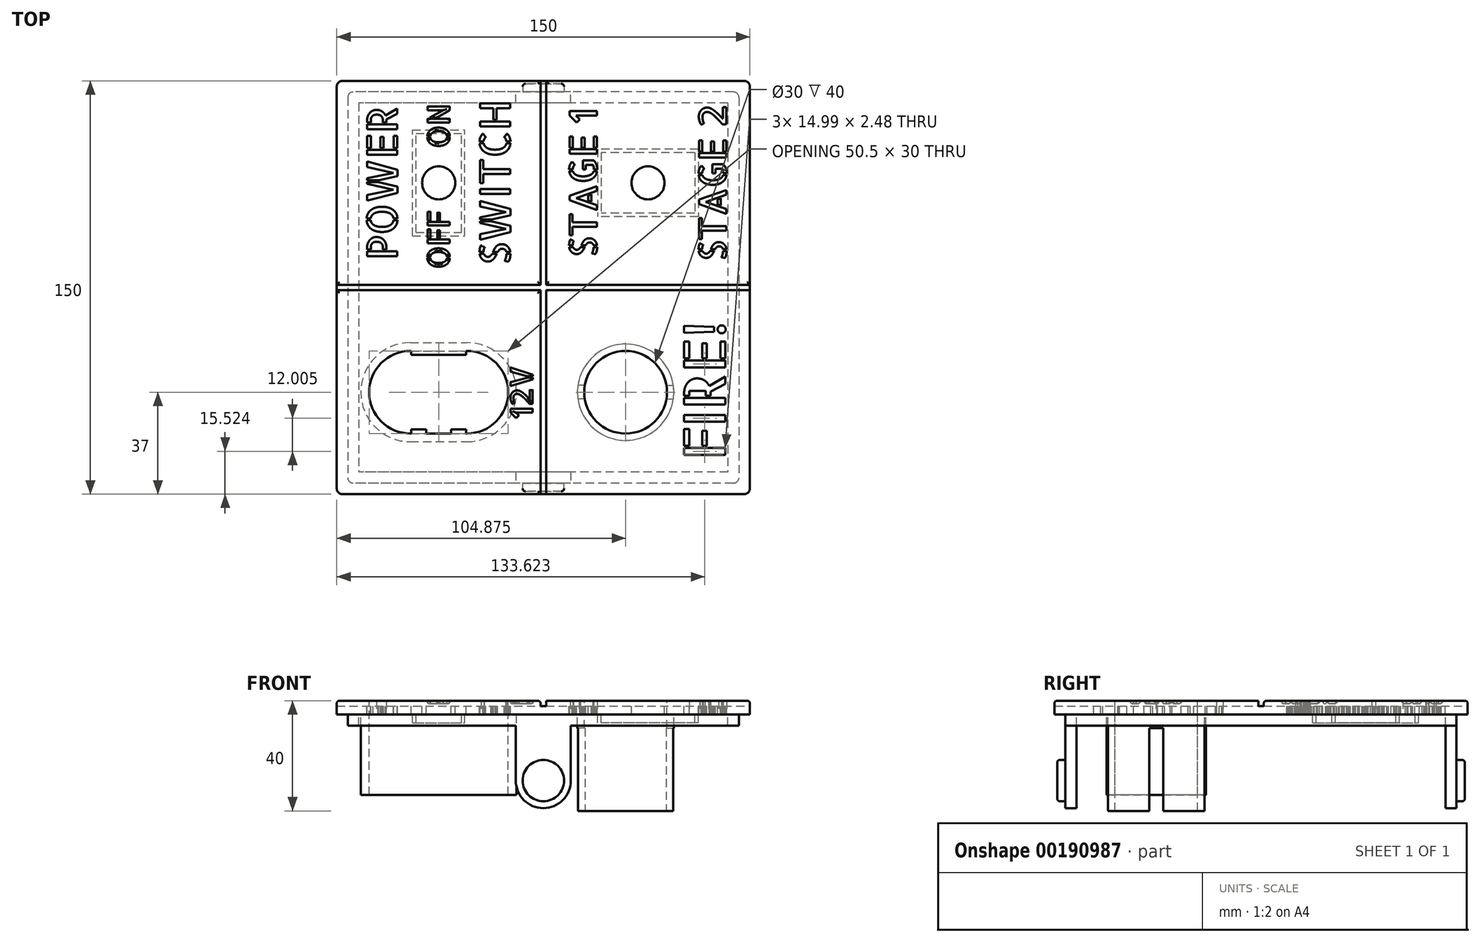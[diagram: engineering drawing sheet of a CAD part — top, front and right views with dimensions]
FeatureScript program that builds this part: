
annotation { "Feature Type Name" : "Feature", "Feature Type Description" : "" }
export const myFeature = defineFeature(function(context is Context, id is Id, definition is map)
    precondition{}
    {
        {
            var Q0;
            Q0=qCreatedBy(makeId("Top.planeOp"),FACE);
            var sketch = newSketch(context, id + "F0", { "sketchPlane" : qUnion([Q0])});
            skLineSegment(sketch, "E0.bottom", {"start": v(75, 75) * mm, "end": v(-75, 75) * mm});
            skLineSegment(sketch, "E0.top", {"start": v(75, -75) * mm, "end": v(-75, -75) * mm});
            skLineSegment(sketch, "E0.left", {"start": v(75, 75) * mm, "end": v(75, -75) * mm});
            skLineSegment(sketch, "E0.right", {"start": v(-75, 75) * mm, "end": v(-75, -75) * mm});
            skPoint(sketch, "E0.middle", {"position": v(0, 0) * mm});
            skSolve(sketch);
        }
        {
            var Q0;
            Q0=makeQuery(id+"F0.imprint","IMPRINT",FACE,{"disambiguationData":[TD([[makeQuery(id+"F0.imprint","IMPRINT",EDGE,{"derivedFrom":sQuery(id+"F0.wireOp",EDGE,"E0.bottom")}),1.0]])]});
            extrude(context, id + "F1", {"entities" : qUnion([Q0]), "depth" : 5 * mm});
        }
        {
            var Q0;
            Q0=makeQuery(id+"F1.opExtrude","CAP_FACE",FACE,{"disambiguationData":[OSD([sQuery(id+"F0.wireOp",EDGE,"E0.bottom"),sQuery(id+"F0.wireOp",EDGE,"E0.top"),sQuery(id+"F0.wireOp",EDGE,"E0.left"),sQuery(id+"F0.wireOp",EDGE,"E0.right")])],"isStart":true});
            var sketch = newSketch(context, id + "F2", { "sketchPlane" : qUnion([Q0])});
            skLineSegment(sketch, "E1.0", {"start": v(-71, -71) * mm, "end": v(-71, 71) * mm});
            skLineSegment(sketch, "E1.1", {"start": v(71, -71) * mm, "end": v(-71, -71) * mm});
            skLineSegment(sketch, "E1.2", {"start": v(71, -71) * mm, "end": v(71, 71) * mm});
            skLineSegment(sketch, "E1.3", {"start": v(71, 71) * mm, "end": v(-71, 71) * mm});
            skLineSegment(sketch, "E2.0", {"start": v(-67, -67) * mm, "end": v(-67, 67) * mm});
            skLineSegment(sketch, "E2.1", {"start": v(67, -67) * mm, "end": v(-67, -67) * mm});
            skLineSegment(sketch, "E2.2", {"start": v(67, -67) * mm, "end": v(67, 67) * mm});
            skLineSegment(sketch, "E2.3", {"start": v(67, 67) * mm, "end": v(-67, 67) * mm});
            skSolve(sketch);
        }
        {
            var Q0;
            Q0=makeQuery(id+"F2.imprint","IMPRINT",FACE,{"disambiguationData":[TD([[makeQuery(id+"F2.imprint","IMPRINT",EDGE,{"derivedFrom":sQuery(id+"F2.wireOp",EDGE,"E1.0")}),-1.0]])]});
            extrude(context, id + "F3", {"entities" : qUnion([Q0]), "operationType" : NewBodyOperationType.ADD, "depth" : 4 * mm});
        }
        {
            var Q0;
            Q0=makeQuery(id+"F3.opExtrude","CAP_FACE",FACE,{"disambiguationData":[OSD([sQuery(id+"F2.wireOp",EDGE,"E1.0"),sQuery(id+"F2.wireOp",EDGE,"E1.1"),sQuery(id+"F2.wireOp",EDGE,"E1.2"),sQuery(id+"F2.wireOp",EDGE,"E1.3"),sQuery(id+"F2.wireOp",EDGE,"E2.0"),sQuery(id+"F2.wireOp",EDGE,"E2.1"),sQuery(id+"F2.wireOp",EDGE,"E2.2"),sQuery(id+"F2.wireOp",EDGE,"E2.3")])],"isStart":false});
            var sketch = newSketch(context, id + "F4", { "sketchPlane" : qUnion([Q0])});
            skLineSegment(sketch, "E3.bottom", {"start": v(-10, -67) * mm, "end": v(10, -67) * mm});
            skLineSegment(sketch, "E3.top", {"start": v(-10, -71) * mm, "end": v(10, -71) * mm});
            skLineSegment(sketch, "E3.left", {"start": v(-10, -67) * mm, "end": v(-10, -71) * mm});
            skLineSegment(sketch, "E3.right", {"start": v(10, -67) * mm, "end": v(10, -71) * mm});
            skLineSegment(sketch, "E4.bottom", {"start": v(-67, 10) * mm, "end": v(-71, 10) * mm});
            skLineSegment(sketch, "E4.top", {"start": v(-67, -10) * mm, "end": v(-71, -10) * mm});
            skLineSegment(sketch, "E4.left", {"start": v(-67, 10) * mm, "end": v(-67, -10) * mm});
            skLineSegment(sketch, "E4.right", {"start": v(-71, 10) * mm, "end": v(-71, -10) * mm});
            skLineSegment(sketch, "E5.bottom", {"start": v(10, 67) * mm, "end": v(-10, 67) * mm});
            skLineSegment(sketch, "E5.top", {"start": v(10, 71) * mm, "end": v(-10, 71) * mm});
            skLineSegment(sketch, "E5.left", {"start": v(10, 67) * mm, "end": v(10, 71) * mm});
            skLineSegment(sketch, "E5.right", {"start": v(-10, 67) * mm, "end": v(-10, 71) * mm});
            skLineSegment(sketch, "E6.bottom", {"start": v(67, 10) * mm, "end": v(71, 10) * mm});
            skLineSegment(sketch, "E6.top", {"start": v(67, -10) * mm, "end": v(71, -10) * mm});
            skLineSegment(sketch, "E6.left", {"start": v(67, 10) * mm, "end": v(67, -10) * mm});
            skLineSegment(sketch, "E6.right", {"start": v(71, 10) * mm, "end": v(71, -10) * mm});
            skSolve(sketch);
        }
        {
            var Q0;
            Q0=makeQuery(id+"F4.imprint","IMPRINT",FACE,{"disambiguationData":[TD([[makeQuery(id+"F4.imprint","IMPRINT",EDGE,{"derivedFrom":sQuery(id+"F4.wireOp",EDGE,"E5.bottom")}),-1.0]])]});
            var Q1;
            Q1=makeQuery(id+"F4.imprint","IMPRINT",FACE,{"disambiguationData":[TD([[makeQuery(id+"F4.imprint","IMPRINT",EDGE,{"derivedFrom":sQuery(id+"F4.wireOp",EDGE,"E3.bottom")}),1.0]])]});
            extrude(context, id + "F5", {"entities" : qUnion([Q0, Q1]), "operationType" : NewBodyOperationType.ADD, "depth" : 30 * mm});
        }
        {
            var Q0;
            Q0=makeQuery(id+"F5.opExtrude","CAP_EDGE",EDGE,{"disambiguationData":[OSD([sQuery(id+"F4.wireOp",EDGE,"E3.left")])],"isStart":false});
            var Q1;
            Q1=makeQuery(id+"F5.opExtrude","CAP_EDGE",EDGE,{"disambiguationData":[OSD([sQuery(id+"F4.wireOp",EDGE,"E3.right")])],"isStart":false});
            var Q2;
            Q2=makeQuery(id+"F5.opExtrude","CAP_EDGE",EDGE,{"disambiguationData":[OSD([sQuery(id+"F4.wireOp",EDGE,"E5.left")])],"isStart":false});
            var Q3;
            Q3=makeQuery(id+"F5.opExtrude","CAP_EDGE",EDGE,{"disambiguationData":[OSD([sQuery(id+"F4.wireOp",EDGE,"E5.right")])],"isStart":false});
            fillet(context, id + "F6", {"entities" : qUnion([Q0, Q1, Q2, Q3]), "radius" : 10 * mm, "tangentPropagation" : true, "allowEdgeOverflow" : false});
        }
        {
            var Q0;
            Q0=makeQuery(id+"F5.boolean.opBoolean","MERGE",FACE,{"derivedFrom":[makeQuery(id+"F3.opExtrude","SWEPT_FACE",FACE,{"disambiguationData":[OSD([sQuery(id+"F2.wireOp",EDGE,"E1.1")])]}),makeQuery(id+"F5.opExtrude","SWEPT_FACE",FACE,{"disambiguationData":[OSD([sQuery(id+"F4.wireOp",EDGE,"E3.top")])]})]});
            var sketch = newSketch(context, id + "F7", { "sketchPlane" : qUnion([Q0])});
            skCircle(sketch, "E7", {"center": v(0, -24) * mm, "radius": 7.5 * mm});
            skSolve(sketch);
        }
        {
            var Q0;
            Q0=makeQuery(id+"F7.imprint","IMPRINT",FACE,{"disambiguationData":[TD([[makeQuery(id+"F7.imprint","IMPRINT",EDGE,{"derivedFrom":sQuery(id+"F7.wireOp",EDGE,"E7")}),1.0]])]});
            extrude(context, id + "F8", {"entities" : qUnion([Q0]), "operationType" : NewBodyOperationType.ADD, "depth" : 3 * mm});
        }
        {
            var Q0;
            Q0=makeQuery(id+"F5.boolean.opBoolean","MERGE",FACE,{"derivedFrom":[makeQuery(id+"F3.opExtrude","SWEPT_FACE",FACE,{"disambiguationData":[OSD([sQuery(id+"F2.wireOp",EDGE,"E1.3")])]}),makeQuery(id+"F5.opExtrude","SWEPT_FACE",FACE,{"disambiguationData":[OSD([sQuery(id+"F4.wireOp",EDGE,"E5.top")])]})]});
            var sketch = newSketch(context, id + "F9", { "sketchPlane" : qUnion([Q0])});
            skCircle(sketch, "E8", {"center": v(0, -24) * mm, "radius": 7.5 * mm});
            skSolve(sketch);
        }
        {
            var Q0;
            Q0=makeQuery(id+"F9.imprint","IMPRINT",FACE,{"disambiguationData":[TD([[makeQuery(id+"F9.imprint","IMPRINT",EDGE,{"derivedFrom":sQuery(id+"F9.wireOp",EDGE,"E8")}),1.0]])]});
            extrude(context, id + "F10", {"entities" : qUnion([Q0]), "operationType" : NewBodyOperationType.ADD, "depth" : 3 * mm});
        }
        {
            var Q0;
            Q0=makeQuery(id+"F10.opExtrude","CAP_EDGE",EDGE,{"disambiguationData":[OSD([sQuery(id+"F9.wireOp",EDGE,"E8")])],"isStart":false});
            var Q1;
            Q1=makeQuery(id+"F8.opExtrude","CAP_EDGE",EDGE,{"disambiguationData":[OSD([sQuery(id+"F7.wireOp",EDGE,"E7")])],"isStart":false});
            fillet(context, id + "F11", {"entities" : qUnion([Q0, Q1]), "radius" : 1 * mm, "tangentPropagation" : true, "allowEdgeOverflow" : false});
        }
        {
            var Q0;
            Q0=makeQuery(id+"F1.opExtrude","CAP_FACE",FACE,{"disambiguationData":[OSD([sQuery(id+"F0.wireOp",EDGE,"E0.bottom"),sQuery(id+"F0.wireOp",EDGE,"E0.top"),sQuery(id+"F0.wireOp",EDGE,"E0.left"),sQuery(id+"F0.wireOp",EDGE,"E0.right")])],"isStart":false});
            var sketch = newSketch(context, id + "F12", { "sketchPlane" : qUnion([Q0])});
            skLineSegment(sketch, "E9", {"start": v(75, 75) * mm, "end": v(0, 75) * mm});
            skCircle(sketch, "E10", {"center": v(38, 38) * mm, "radius": 6 * mm});
            skCircle(sketch, "E11", {"center": v(29.87, -38) * mm, "radius": 15 * mm});
            skLineSegment(sketch, "E12", {"start": v(38, -38) * mm, "end": v(29.87, -38) * mm});
            skCircle(sketch, "E13", {"center": v(-38, 38) * mm, "radius": 6 * mm});
            skLineSegment(sketch, "E14.0", {"start": v(1, -75) * mm, "end": v(1, -1) * mm});
            skLineSegment(sketch, "E15.0", {"start": v(-1, -75) * mm, "end": v(-1, -1) * mm});
            skLineSegment(sketch, "E16.0", {"start": v(-75, -1) * mm, "end": v(-1, -1) * mm});
            skLineSegment(sketch, "E17.0", {"start": v(-75, 1) * mm, "end": v(-1, 1) * mm});
            skLineSegment(sketch, "E18.trimOffspring", {"start": v(-1, 1) * mm, "end": v(-1, 75) * mm});
            skLineSegment(sketch, "E19.trimOffspring", {"start": v(1, 1) * mm, "end": v(75, 1) * mm});
            skLineSegment(sketch, "E20.trimOffspring", {"start": v(1, -1) * mm, "end": v(75, -1) * mm});
            skLineSegment(sketch, "E21.trimOffspring", {"start": v(1, 1) * mm, "end": v(1, 75) * mm});
            skLineSegment(sketch, "E22.bottom", {"start": v(-48.25, -53) * mm, "end": v(-27.75, -53) * mm});
            skLineSegment(sketch, "E22.top", {"start": v(-48.25, -23) * mm, "end": v(-27.75, -23) * mm});
            skArc(sketch, "E23", {"start": v(-48.25, -23) * mm, "mid": v(-63.25, -38) * mm, "end": v(-48.25, -53) * mm});
            skArc(sketch, "E24", {"start": v(-27.75, -53) * mm, "mid": v(-12.75, -38) * mm, "end": v(-27.75, -23) * mm});
            skPoint(sketch, "E25", {"position": v(-63.25, -38) * mm});
            skPoint(sketch, "E26", {"position": v(-12.75, -38) * mm});
            skArc(sketch, "E27.0", {"start": v(-48.25, -20) * mm, "mid": v(-66.25, -38) * mm, "end": v(-48.25, -56) * mm});
            skLineSegment(sketch, "E27.1", {"start": v(-48.25, -20) * mm, "end": v(-27.75, -20) * mm});
            skArc(sketch, "E27.2", {"start": v(-27.75, -56) * mm, "mid": v(-9.75, -38) * mm, "end": v(-27.75, -20) * mm});
            skLineSegment(sketch, "E27.3", {"start": v(-48.25, -56) * mm, "end": v(-27.75, -56) * mm});
            skPoint(sketch, "E28", {"position": v(-38, -38) * mm});
            skPoint(sketch, "E29", {"position": v(-38, -23) * mm});
            skPoint(sketch, "E30", {"position": v(-38, -53) * mm});
            skLineSegment(sketch, "E31.bottom", {"start": v(-48, -24.5) * mm, "end": v(-28, -24.5) * mm});
            skLineSegment(sketch, "E31.left", {"start": v(-48, -24.5) * mm, "end": v(-48, -23) * mm});
            skLineSegment(sketch, "E31.right", {"start": v(-28, -24.5) * mm, "end": v(-28, -23) * mm});
            skLineSegment(sketch, "E32.bottom", {"start": v(-48, -51.5) * mm, "end": v(-42.5, -51.5) * mm});
            skLineSegment(sketch, "E32.left", {"start": v(-48, -51.5) * mm, "end": v(-48, -53) * mm});
            skLineSegment(sketch, "E32.right", {"start": v(-28, -51.5) * mm, "end": v(-28, -53) * mm});
            skLineSegment(sketch, "E33.left", {"start": v(-42.5, -51.5) * mm, "end": v(-42.5, -53) * mm});
            skLineSegment(sketch, "E33.right", {"start": v(-33.5, -51.5) * mm, "end": v(-33.5, -53) * mm});
            skLineSegment(sketch, "E34.trimOffspring", {"start": v(-33.5, -51.5) * mm, "end": v(-28, -51.5) * mm});
            skSolve(sketch);
        }
        {
            var Q0;
            Q0=makeQuery(id+"F12.imprint","IMPRINT",FACE,{"disambiguationData":[TD([[makeQuery(id+"F12.imprint","IMPRINT",EDGE,{"derivedFrom":sQuery(id+"F12.wireOp",EDGE,"E10")}),1.0]])]});
            var Q1;
            Q1=makeQuery(id+"F12.imprint","IMPRINT",FACE,{"disambiguationData":[TD([[makeQuery(id+"F12.imprint","IMPRINT",EDGE,{"derivedFrom":sQuery(id+"F12.wireOp",EDGE,"E11")}),1.0]])]});
            var Q2;
            Q2=makeQuery(id+"F12.imprint","IMPRINT",FACE,{"disambiguationData":[TD([[makeQuery(id+"F12.imprint","IMPRINT",EDGE,{"derivedFrom":sQuery(id+"F12.wireOp",EDGE,"E13")}),1.0]])]});
            var Q3;
            Q3=makeQuery(id+"F12.imprint","IMPRINT",FACE,{"disambiguationData":[TD([[makeQuery(id+"F12.imprint","IMPRINT",EDGE,{"derivedFrom":sQuery(id+"F12.wireOp",EDGE,"E22.bottom")}),1.0]])]});
            extrude(context, id + "F13", {"entities" : qUnion([Q0, Q1, Q2, Q3]), "operationType" : NewBodyOperationType.REMOVE, "oppositeDirection" : true, "depth" : 25 * mm});
        }
        {
            var Q0;
            Q0=makeQuery(id+"F3.boolean.opBoolean","SPLIT",FACE,{"disambiguationData":[TD([makeQuery(id+"F3.opExtrude","SWEPT_FACE",FACE,{"disambiguationData":[OSD([sQuery(id+"F2.wireOp",EDGE,"E2.0")])]})])],"derivedFrom":makeQuery(id+"F1.opExtrude","CAP_FACE",FACE,{"disambiguationData":[OSD([sQuery(id+"F0.wireOp",EDGE,"E0.bottom"),sQuery(id+"F0.wireOp",EDGE,"E0.top"),sQuery(id+"F0.wireOp",EDGE,"E0.left"),sQuery(id+"F0.wireOp",EDGE,"E0.right")])],"isStart":true})});
            var sketch = newSketch(context, id + "F14", { "sketchPlane" : qUnion([Q0])});
            skLineSegment(sketch, "E35.bottom", {"start": v(55, -49) * mm, "end": v(21, -49) * mm});
            skLineSegment(sketch, "E35.top", {"start": v(55, -27) * mm, "end": v(21, -27) * mm});
            skLineSegment(sketch, "E35.left", {"start": v(55, -49) * mm, "end": v(55, -27) * mm});
            skLineSegment(sketch, "E35.right", {"start": v(21, -49) * mm, "end": v(21, -27) * mm});
            skPoint(sketch, "E35.middle", {"position": v(38, -38) * mm});
            skLineSegment(sketch, "E36.0", {"start": v(19.75, -50.25) * mm, "end": v(19.75, -25.75) * mm});
            skLineSegment(sketch, "E36.1", {"start": v(56.25, -50.25) * mm, "end": v(19.75, -50.25) * mm});
            skLineSegment(sketch, "E36.2", {"start": v(56.25, -50.25) * mm, "end": v(56.25, -25.75) * mm});
            skLineSegment(sketch, "E36.3", {"start": v(56.25, -25.75) * mm, "end": v(19.75, -25.75) * mm});
            skCircle(sketch, "E37", {"center": v(29.87, 38) * mm, "radius": 15 * mm});
            skCircle(sketch, "E38", {"center": v(29.87, 38) * mm, "radius": 17.5 * mm});
            skPoint(sketch, "E39.middle", {"position": v(-38, -38) * mm});
            skLineSegment(sketch, "E40.bottom", {"start": v(-46.25, -20) * mm, "end": v(-29.75, -20) * mm});
            skLineSegment(sketch, "E40.top", {"start": v(-46.25, -56) * mm, "end": v(-29.75, -56) * mm});
            skLineSegment(sketch, "E40.left", {"start": v(-46.25, -20) * mm, "end": v(-46.25, -56) * mm});
            skLineSegment(sketch, "E40.right", {"start": v(-29.75, -20) * mm, "end": v(-29.75, -56) * mm});
            skLineSegment(sketch, "E41.0", {"start": v(-47.5, -18.75) * mm, "end": v(-47.5, -57.25) * mm});
            skLineSegment(sketch, "E41.1", {"start": v(-47.5, -18.75) * mm, "end": v(-28.5, -18.75) * mm});
            skLineSegment(sketch, "E41.2", {"start": v(-28.5, -18.75) * mm, "end": v(-28.5, -57.25) * mm});
            skLineSegment(sketch, "E41.3", {"start": v(-47.5, -57.25) * mm, "end": v(-28.5, -57.25) * mm});
            skSolve(sketch);
        }
        {
            var Q0;
            Q0=makeQuery(id+"F14.imprint","IMPRINT",FACE,{"disambiguationData":[TD([[makeQuery(id+"F14.imprint","IMPRINT",EDGE,{"derivedFrom":sQuery(id+"F14.wireOp",EDGE,"E35.bottom")}),1.0]])]});
            var Q1;
            Q1=makeQuery(id+"F14.imprint","IMPRINT",FACE,{"disambiguationData":[TD([[makeQuery(id+"F14.imprint","IMPRINT",EDGE,{"derivedFrom":sQuery(id+"F14.wireOp",EDGE,"E39.bottom")}),1.0]])]});
            var Q2;
            Q2=makeQuery(id+"F14.imprint","IMPRINT",FACE,{"disambiguationData":[TD([[makeQuery(id+"F14.imprint","IMPRINT",EDGE,{"derivedFrom":sQuery(id+"F14.wireOp",EDGE,"E39.top")}),-1.0]])]});
            var Q3;
            Q3=makeQuery(id+"F14.imprint","IMPRINT",FACE,{"disambiguationData":[TD([[makeQuery(id+"F14.imprint","IMPRINT",EDGE,{"derivedFrom":sQuery(id+"F14.wireOp",EDGE,"E40.bottom")}),1.0]])]});
            extrude(context, id + "F15", {"entities" : qUnion([Q0, Q1, Q2, Q3]), "operationType" : NewBodyOperationType.ADD, "depth" : 3 * mm});
        }
        {
            var Q0;
            Q0=makeQuery(id+"F1.opExtrude","CAP_FACE",FACE,{"disambiguationData":[OSD([sQuery(id+"F0.wireOp",EDGE,"E0.bottom"),sQuery(id+"F0.wireOp",EDGE,"E0.top"),sQuery(id+"F0.wireOp",EDGE,"E0.left"),sQuery(id+"F0.wireOp",EDGE,"E0.right")])],"isStart":false});
            var sketch = newSketch(context, id + "F16", { "sketchPlane" : qUnion([Q0])});
            skCircle(sketch, "E42", {"center": v(38, 38) * mm, "radius": 6 * mm});
            skLineSegment(sketch, "E43", {"start": v(38, 38) * mm, "end": v(32, 38) * mm});
            skLineSegment(sketch, "E44", {"start": v(38, 38) * mm, "end": v(44, 38) * mm});
            skLineSegment(sketch, "E45", {"start": v(44, 38) * mm, "end": v(56.5, 38) * mm});
            skLineSegment(sketch, "E46", {"start": v(32, 38) * mm, "end": v(19.5, 38) * mm});
            skText(sketch, "E47", { "text": "STAGE 2", "fontName": "AllertaStencil-Regular.ttf"});
            skText(sketch, "E48", { "text": "STAGE 1", "fontName": "AllertaStencil-Regular.ttf"});
            skText(sketch, "E49", { "text": "FIRE!", "fontName": "AllertaStencil-Regular.ttf"});
            skLineSegment(sketch, "E50", {"start": v(44.87, -37.48) * mm, "end": v(51.12, -37.48) * mm});
            skPoint(sketch, "E51", {"position": v(58.62, -37.48) * mm});
            skLineSegment(sketch, "E52", {"start": v(66.12, -37.48) * mm, "end": v(44.87, -37.48) * mm});
            skPoint(sketch, "E53", {"position": v(40.5, -37.48) * mm});
            skLineSegment(sketch, "E54", {"start": v(0, -75) * mm, "end": v(75, 0) * mm});
            skLineSegment(sketch, "E55", {"start": v(75, -75) * mm, "end": v(0, 0) * mm});
            skPoint(sketch, "E56.orphan", {"position": v(14.88, -37.48) * mm});
            skLineSegment(sketch, "E57.trimOffspring", {"start": v(40.5, -37.48) * mm, "end": v(37.52, -37.48) * mm});
            skText(sketch, "E58", { "text": "POWER", "fontName": "AllertaStencil-Regular.ttf"});
            skLineSegment(sketch, "E59", {"start": v(-38, 38) * mm, "end": v(-53, 38) * mm});
            skLineSegment(sketch, "E60", {"start": v(-38, 38) * mm, "end": v(-23, 38) * mm});
            skText(sketch, "E61", { "text": "SWITCH", "fontName": "AllertaStencil-Regular.ttf"});
            const initialGuessF16  = {"E47": [0.0665, 0.00959, 0, 1, 0.01], "E48": [0.0195, 0.01099, 0, 1, 0.01], "E49": [0.06612, -0.06265, 0, 1, 0.015], "E58": [-0.053, 0.01, 0, 1, 0.011], "E61": [-0.012, 0.00816, 0, 1, 0.011]};
            skSetInitialGuess(sketch, initialGuessF16);
            skSolve(sketch);
        }
        {
            var Q0;
            Q0 = qSketchRegion(id + "F16", true);
            extrude(context, id + "F17", {"entities" : qUnion([Q0]), "operationType" : NewBodyOperationType.REMOVE, "oppositeDirection" : true, "depth" : 25 * mm});
        }
        {
            var Q0;
            Q0=makeQuery(id+"F14.imprint","IMPRINT",FACE,{"disambiguationData":[TD([[makeQuery(id+"F14.imprint","IMPRINT",EDGE,{"derivedFrom":sQuery(id+"F14.wireOp",EDGE,"E37")}),1.0]])]});
            extrude(context, id + "F18", {"entities" : qUnion([Q0]), "operationType" : NewBodyOperationType.ADD, "depth" : 35 * mm});
        }
        {
            var Q0;
            Q0=makeQuery(id+"F18.opExtrude","CAP_FACE",FACE,{"disambiguationData":[OSD([sQuery(id+"F14.wireOp",EDGE,"E37"),sQuery(id+"F14.wireOp",EDGE,"E38")])],"isStart":false});
            var sketch = newSketch(context, id + "F19", { "sketchPlane" : qUnion([Q0])});
            skCircle(sketch, "E62", {"center": v(29.87, 38) * mm, "radius": 16.25 * mm});
            skPoint(sketch, "E63", {"position": v(46.12, 38) * mm});
            skPoint(sketch, "E64", {"position": v(13.62, 38) * mm});
            skLineSegment(sketch, "E65.bottom", {"start": v(15.62, 35.5) * mm, "end": v(11.62, 35.5) * mm});
            skLineSegment(sketch, "E65.top", {"start": v(15.62, 40.5) * mm, "end": v(11.62, 40.5) * mm});
            skLineSegment(sketch, "E65.left", {"start": v(15.62, 35.5) * mm, "end": v(15.62, 40.5) * mm});
            skLineSegment(sketch, "E65.right", {"start": v(11.62, 35.5) * mm, "end": v(11.62, 40.5) * mm});
            skLineSegment(sketch, "E66.bottom", {"start": v(44.12, 35.5) * mm, "end": v(48.12, 35.5) * mm});
            skLineSegment(sketch, "E66.top", {"start": v(44.12, 40.5) * mm, "end": v(48.12, 40.5) * mm});
            skLineSegment(sketch, "E66.left", {"start": v(44.12, 35.5) * mm, "end": v(44.12, 40.5) * mm});
            skLineSegment(sketch, "E66.right", {"start": v(48.12, 35.5) * mm, "end": v(48.12, 40.5) * mm});
            skSolve(sketch);
        }
        {
            var Q0;
            {var subQ0=sQuery(id+"F19.wireOp",EDGE,"E65.top");var subQ1=sQuery(id+"F19.wireOp",EDGE,"E62");var subQ2=makeQuery(id+"F19.imprint","INTERSECT",VERTEX,{"derivedFrom":[subQ1,subQ0]});Q0=makeQuery(id+"F19.imprint","IMPRINT",FACE,{"disambiguationData":[TD([[makeQuery(id+"F19.imprint","IMPRINT",EDGE,{"disambiguationData":[TD([[subQ2,-1.0]])],"derivedFrom":subQ1}),1.0]])]});}
            var Q1;
            {var subQ0=sQuery(id+"F19.wireOp",EDGE,"E65.top");var subQ1=sQuery(id+"F19.wireOp",EDGE,"E62");var subQ2=makeQuery(id+"F19.imprint","INTERSECT",VERTEX,{"derivedFrom":[subQ1,subQ0]});Q1=makeQuery(id+"F19.imprint","IMPRINT",FACE,{"disambiguationData":[TD([[makeQuery(id+"F19.imprint","IMPRINT",EDGE,{"disambiguationData":[TD([[subQ2,-1.0]])],"derivedFrom":subQ1}),-1.0]])]});}
            var Q2;
            {var subQ0=sQuery(id+"F19.wireOp",EDGE,"E66.top");var subQ1=sQuery(id+"F19.wireOp",EDGE,"E62");var subQ2=makeQuery(id+"F19.imprint","INTERSECT",VERTEX,{"derivedFrom":[subQ1,subQ0]});Q2=makeQuery(id+"F19.imprint","IMPRINT",FACE,{"disambiguationData":[TD([[makeQuery(id+"F19.imprint","IMPRINT",EDGE,{"disambiguationData":[TD([[subQ2,1.0]])],"derivedFrom":subQ1}),1.0]])]});}
            var Q3;
            {var subQ0=sQuery(id+"F19.wireOp",EDGE,"E66.top");var subQ1=sQuery(id+"F19.wireOp",EDGE,"E62");var subQ2=makeQuery(id+"F19.imprint","INTERSECT",VERTEX,{"derivedFrom":[subQ1,subQ0]});Q3=makeQuery(id+"F19.imprint","IMPRINT",FACE,{"disambiguationData":[TD([[makeQuery(id+"F19.imprint","IMPRINT",EDGE,{"disambiguationData":[TD([[subQ2,1.0]])],"derivedFrom":subQ1}),-1.0]])]});}
            extrude(context, id + "F20", {"entities" : qUnion([Q0, Q1, Q2, Q3]), "operationType" : NewBodyOperationType.REMOVE, "oppositeDirection" : true, "depth" : 30 * mm});
        }
        {
            var Q0;
            {var subQ8=sQuery(id+"F12.wireOp",EDGE,"E14.0");Q0=makeQuery(id+"F12.imprint","IMPRINT",FACE,{"disambiguationData":[TD([[makeQuery(id+"F12.imprint","IMPRINT",EDGE,{"derivedFrom":subQ8}),1.0]])]});}
            extrude(context, id + "F21", {"entities" : qUnion([Q0]), "operationType" : NewBodyOperationType.REMOVE, "oppositeDirection" : true, "depth" : 2 * mm});
        }
        {
            var Q0;
            Q0=makeQuery(id+"F21.boolean.opBoolean","COPY",EDGE,{"derivedFrom":makeQuery(id+"F21.opExtrude","CAP_EDGE",EDGE,{"disambiguationData":[OSD([sQuery(id+"F12.wireOp",EDGE,"E20.trimOffspring")])],"isStart":true})});
            var Q1;
            Q1=makeQuery(id+"F21.boolean.opBoolean","COPY",EDGE,{"derivedFrom":makeQuery(id+"F21.opExtrude","CAP_EDGE",EDGE,{"disambiguationData":[OSD([sQuery(id+"F12.wireOp",EDGE,"E16.0")])],"isStart":true})});
            var Q2;
            Q2=makeQuery(id+"F21.boolean.opBoolean","COPY",EDGE,{"derivedFrom":makeQuery(id+"F21.opExtrude","CAP_EDGE",EDGE,{"disambiguationData":[OSD([sQuery(id+"F12.wireOp",EDGE,"E15.0")])],"isStart":true})});
            var Q3;
            Q3=makeQuery(id+"F21.boolean.opBoolean","COPY",EDGE,{"derivedFrom":makeQuery(id+"F21.opExtrude","CAP_EDGE",EDGE,{"disambiguationData":[OSD([sQuery(id+"F12.wireOp",EDGE,"E17.0")])],"isStart":true})});
            var Q4;
            Q4=makeQuery(id+"F21.boolean.opBoolean","COPY",EDGE,{"derivedFrom":makeQuery(id+"F21.opExtrude","CAP_EDGE",EDGE,{"disambiguationData":[OSD([sQuery(id+"F12.wireOp",EDGE,"E18.trimOffspring")])],"isStart":true})});
            var Q5;
            Q5=makeQuery(id+"F21.boolean.opBoolean","COPY",EDGE,{"derivedFrom":makeQuery(id+"F21.opExtrude","CAP_EDGE",EDGE,{"disambiguationData":[OSD([sQuery(id+"F12.wireOp",EDGE,"E21.trimOffspring")])],"isStart":true})});
            var Q6;
            Q6=makeQuery(id+"F21.boolean.opBoolean","COPY",EDGE,{"derivedFrom":makeQuery(id+"F21.opExtrude","CAP_EDGE",EDGE,{"disambiguationData":[OSD([sQuery(id+"F12.wireOp",EDGE,"E19.trimOffspring")])],"isStart":true})});
            var Q7;
            Q7=makeQuery(id+"F21.boolean.opBoolean","COPY",EDGE,{"derivedFrom":makeQuery(id+"F21.opExtrude","CAP_EDGE",EDGE,{"disambiguationData":[OSD([sQuery(id+"F12.wireOp",EDGE,"E14.0")])],"isStart":true})});
            var Q8;
            {var subQ0=sQuery(id+"F0.wireOp",EDGE,"E0.bottom");var subQ1=sQuery(id+"F0.wireOp",EDGE,"E0.right");Q8=makeQuery(id+"F21.boolean.opBoolean","SPLIT",EDGE,{"disambiguationData":[TD([makeQuery(id+"F1.opExtrude","SWEPT_FACE",FACE,{"disambiguationData":[OSD([subQ1])]})])],"derivedFrom":makeQuery(id+"F1.opExtrude","CAP_EDGE",EDGE,{"disambiguationData":[OSD([subQ0])],"isStart":false})});}
            var Q9;
            {var subQ0=sQuery(id+"F0.wireOp",EDGE,"E0.bottom");var subQ1=sQuery(id+"F0.wireOp",EDGE,"E0.left");Q9=makeQuery(id+"F21.boolean.opBoolean","SPLIT",EDGE,{"disambiguationData":[TD([makeQuery(id+"F1.opExtrude","SWEPT_FACE",FACE,{"disambiguationData":[OSD([subQ1])]})])],"derivedFrom":makeQuery(id+"F1.opExtrude","CAP_EDGE",EDGE,{"disambiguationData":[OSD([subQ0])],"isStart":false})});}
            var Q10;
            {var subQ0=sQuery(id+"F0.wireOp",EDGE,"E0.bottom");var subQ1=sQuery(id+"F0.wireOp",EDGE,"E0.left");Q10=makeQuery(id+"F21.boolean.opBoolean","SPLIT",EDGE,{"disambiguationData":[TD([makeQuery(id+"F1.opExtrude","SWEPT_FACE",FACE,{"disambiguationData":[OSD([subQ0])]})])],"derivedFrom":makeQuery(id+"F1.opExtrude","CAP_EDGE",EDGE,{"disambiguationData":[OSD([subQ1])],"isStart":false})});}
            var Q11;
            {var subQ0=sQuery(id+"F0.wireOp",EDGE,"E0.left");var subQ1=sQuery(id+"F0.wireOp",EDGE,"E0.top");Q11=makeQuery(id+"F21.boolean.opBoolean","SPLIT",EDGE,{"disambiguationData":[TD([makeQuery(id+"F1.opExtrude","SWEPT_FACE",FACE,{"disambiguationData":[OSD([subQ1])]})])],"derivedFrom":makeQuery(id+"F1.opExtrude","CAP_EDGE",EDGE,{"disambiguationData":[OSD([subQ0])],"isStart":false})});}
            var Q12;
            {var subQ0=sQuery(id+"F0.wireOp",EDGE,"E0.left");var subQ1=sQuery(id+"F0.wireOp",EDGE,"E0.top");Q12=makeQuery(id+"F21.boolean.opBoolean","SPLIT",EDGE,{"disambiguationData":[TD([makeQuery(id+"F1.opExtrude","SWEPT_FACE",FACE,{"disambiguationData":[OSD([subQ0])]})])],"derivedFrom":makeQuery(id+"F1.opExtrude","CAP_EDGE",EDGE,{"disambiguationData":[OSD([subQ1])],"isStart":false})});}
            var Q13;
            {var subQ0=sQuery(id+"F0.wireOp",EDGE,"E0.right");var subQ1=sQuery(id+"F0.wireOp",EDGE,"E0.top");Q13=makeQuery(id+"F21.boolean.opBoolean","SPLIT",EDGE,{"disambiguationData":[TD([makeQuery(id+"F1.opExtrude","SWEPT_FACE",FACE,{"disambiguationData":[OSD([subQ0])]})])],"derivedFrom":makeQuery(id+"F1.opExtrude","CAP_EDGE",EDGE,{"disambiguationData":[OSD([subQ1])],"isStart":false})});}
            var Q14;
            {var subQ0=sQuery(id+"F0.wireOp",EDGE,"E0.right");var subQ1=sQuery(id+"F0.wireOp",EDGE,"E0.top");Q14=makeQuery(id+"F21.boolean.opBoolean","SPLIT",EDGE,{"disambiguationData":[TD([makeQuery(id+"F1.opExtrude","SWEPT_FACE",FACE,{"disambiguationData":[OSD([subQ1])]})])],"derivedFrom":makeQuery(id+"F1.opExtrude","CAP_EDGE",EDGE,{"disambiguationData":[OSD([subQ0])],"isStart":false})});}
            var Q15;
            {var subQ0=sQuery(id+"F0.wireOp",EDGE,"E0.bottom");var subQ1=sQuery(id+"F0.wireOp",EDGE,"E0.right");Q15=makeQuery(id+"F21.boolean.opBoolean","SPLIT",EDGE,{"disambiguationData":[TD([makeQuery(id+"F1.opExtrude","SWEPT_FACE",FACE,{"disambiguationData":[OSD([subQ0])]})])],"derivedFrom":makeQuery(id+"F1.opExtrude","CAP_EDGE",EDGE,{"disambiguationData":[OSD([subQ1])],"isStart":false})});}
            fillet(context, id + "F22", {"entities" : qUnion([Q0, Q1, Q2, Q3, Q4, Q5, Q6, Q7, Q8, Q9, Q10, Q11, Q12, Q13, Q14, Q15]), "radius" : 1 * mm, "tangentPropagation" : true, "allowEdgeOverflow" : false});
        }
        {
            var Q0;
            Q0=makeQuery(id+"F1.opExtrude","CAP_EDGE",EDGE,{"disambiguationData":[OSD([sQuery(id+"F0.wireOp",EDGE,"E0.top")])],"isStart":false});
            var Q1;
            Q1=makeQuery(id+"F1.opExtrude","CAP_EDGE",EDGE,{"disambiguationData":[OSD([sQuery(id+"F0.wireOp",EDGE,"E0.left")])],"isStart":false});
            var Q2;
            Q2=makeQuery(id+"F1.opExtrude","CAP_EDGE",EDGE,{"disambiguationData":[OSD([sQuery(id+"F0.wireOp",EDGE,"E0.bottom")])],"isStart":false});
            var Q3;
            Q3=makeQuery(id+"F1.opExtrude","CAP_EDGE",EDGE,{"disambiguationData":[OSD([sQuery(id+"F0.wireOp",EDGE,"E0.right")])],"isStart":false});
            var Q4;
            Q4=makeQuery(id+"F1.opExtrude","SWEPT_EDGE",EDGE,{"disambiguationData":[OSD([sQuery(id+"F0.wireOp",EDGE,"E0.top"),sQuery(id+"F0.wireOp",EDGE,"E0.right")])]});
            var Q5;
            Q5=makeQuery(id+"F1.opExtrude","SWEPT_EDGE",EDGE,{"disambiguationData":[OSD([sQuery(id+"F0.wireOp",EDGE,"E0.bottom"),sQuery(id+"F0.wireOp",EDGE,"E0.right")])]});
            var Q6;
            Q6=makeQuery(id+"F1.opExtrude","SWEPT_EDGE",EDGE,{"disambiguationData":[OSD([sQuery(id+"F0.wireOp",EDGE,"E0.bottom"),sQuery(id+"F0.wireOp",EDGE,"E0.left")])]});
            var Q7;
            Q7=makeQuery(id+"F1.opExtrude","SWEPT_EDGE",EDGE,{"disambiguationData":[OSD([sQuery(id+"F0.wireOp",EDGE,"E0.top"),sQuery(id+"F0.wireOp",EDGE,"E0.left")])]});
            var Q8;
            Q8=makeQuery(id+"F3.opExtrude","SWEPT_EDGE",EDGE,{"disambiguationData":[OSD([sQuery(id+"F2.wireOp",EDGE,"E1.2"),sQuery(id+"F2.wireOp",EDGE,"E1.3")])]});
            var Q9;
            Q9=makeQuery(id+"F3.opExtrude","SWEPT_EDGE",EDGE,{"disambiguationData":[OSD([sQuery(id+"F2.wireOp",EDGE,"E1.1"),sQuery(id+"F2.wireOp",EDGE,"E1.2")])]});
            var Q10;
            Q10=makeQuery(id+"F3.opExtrude","SWEPT_EDGE",EDGE,{"disambiguationData":[OSD([sQuery(id+"F2.wireOp",EDGE,"E1.0"),sQuery(id+"F2.wireOp",EDGE,"E1.1")])]});
            var Q11;
            Q11=makeQuery(id+"F3.opExtrude","SWEPT_EDGE",EDGE,{"disambiguationData":[OSD([sQuery(id+"F2.wireOp",EDGE,"E1.0"),sQuery(id+"F2.wireOp",EDGE,"E1.3")])]});
            var Q12;
            Q12=makeQuery(id+"F20.boolean.opBoolean","COPY",EDGE,{"derivedFrom":makeQuery(id+"F20.opExtrude","SWEPT_EDGE",EDGE,{"disambiguationData":[OSD([sQuery(id+"F14.wireOp",EDGE,"E37"),sQuery(id+"F19.wireOp",EDGE,"E66.top")])]})});
            var Q13;
            Q13=makeQuery(id+"F20.boolean.opBoolean","COPY",EDGE,{"derivedFrom":makeQuery(id+"F20.opExtrude","SWEPT_EDGE",EDGE,{"disambiguationData":[OSD([sQuery(id+"F14.wireOp",EDGE,"E37"),sQuery(id+"F19.wireOp",EDGE,"E65.top")])]})});
            var Q14;
            Q14=makeQuery(id+"F20.boolean.opBoolean","COPY",EDGE,{"derivedFrom":makeQuery(id+"F20.opExtrude","SWEPT_EDGE",EDGE,{"disambiguationData":[OSD([sQuery(id+"F14.wireOp",EDGE,"E37"),sQuery(id+"F19.wireOp",EDGE,"E65.bottom")])]})});
            var Q15;
            Q15=makeQuery(id+"F20.boolean.opBoolean","COPY",EDGE,{"derivedFrom":makeQuery(id+"F20.opExtrude","SWEPT_EDGE",EDGE,{"disambiguationData":[OSD([sQuery(id+"F14.wireOp",EDGE,"E37"),sQuery(id+"F19.wireOp",EDGE,"E66.bottom")])]})});
            var Q16;
            {var subQ0=sQuery(id+"F14.wireOp",EDGE,"E37");var subQ1=makeQuery(id+"F18.opExtrude","CAP_EDGE",EDGE,{"disambiguationData":[OSD([subQ0])],"isStart":false});Q16=makeQuery(id+"F20.boolean.opBoolean","COPY",EDGE,{"derivedFrom":makeQuery(id+"F20.opExtrude","CAP_EDGE",EDGE,{"disambiguationData":[OSD([subQ0]),TDD([makeQuery(id+"F19.imprint","IMPRINT",EDGE,{"disambiguationData":[TD([[makeQuery(id+"F19.imprint","INTERSECT",VERTEX,{"derivedFrom":[subQ1,sQuery(id+"F19.wireOp",EDGE,"E65.bottom")]}),-1.0]])],"derivedFrom":subQ1})])],"isStart":false})});}
            var Q17;
            {var subQ0=sQuery(id+"F14.wireOp",EDGE,"E37");var subQ1=makeQuery(id+"F18.opExtrude","CAP_EDGE",EDGE,{"disambiguationData":[OSD([subQ0])],"isStart":false});Q17=makeQuery(id+"F20.boolean.opBoolean","COPY",EDGE,{"derivedFrom":makeQuery(id+"F20.opExtrude","CAP_EDGE",EDGE,{"disambiguationData":[OSD([subQ0]),TDD([makeQuery(id+"F19.imprint","IMPRINT",EDGE,{"disambiguationData":[TD([[makeQuery(id+"F19.imprint","INTERSECT",VERTEX,{"derivedFrom":[subQ1,sQuery(id+"F19.wireOp",EDGE,"E66.bottom")]}),1.0]])],"derivedFrom":subQ1})])],"isStart":false})});}
            fillet(context, id + "F23", {"entities" : qUnion([Q0, Q1, Q2, Q3, Q4, Q5, Q6, Q7, Q8, Q9, Q10, Q11, Q12, Q13, Q14, Q15, Q16, Q17]), "radius" : 2 * mm, "tangentPropagation" : true, "allowEdgeOverflow" : false});
        }
        {
            var Q0;
            Q0=makeQuery(id+"F12.imprint","IMPRINT",FACE,{"disambiguationData":[TD([[makeQuery(id+"F12.imprint","IMPRINT",EDGE,{"derivedFrom":sQuery(id+"F12.wireOp",EDGE,"E22.bottom")}),-1.0]])]});
            extrude(context, id + "F24", {"entities" : qUnion([Q0]), "operationType" : NewBodyOperationType.ADD, "oppositeDirection" : true, "depth" : 34.2 * mm});
        }
        {
            var Q0;
            {var subQ0=sQuery(id+"F0.wireOp",EDGE,"E0.bottom");var subQ1=sQuery(id+"F0.wireOp",EDGE,"E0.right");Q0=makeQuery(id+"F21.boolean.opBoolean","SPLIT",FACE,{"disambiguationData":[TD([makeQuery(id+"F13.boolean.opBoolean","COPY",FACE,{"derivedFrom":makeQuery(id+"F13.opExtrude","SWEPT_FACE",FACE,{"disambiguationData":[OSD([sQuery(id+"F12.wireOp",EDGE,"E13")])]})})])],"derivedFrom":makeQuery(id+"F1.opExtrude","CAP_FACE",FACE,{"disambiguationData":[OSD([subQ0,sQuery(id+"F0.wireOp",EDGE,"E0.top"),sQuery(id+"F0.wireOp",EDGE,"E0.left"),subQ1])],"isStart":false})});}
            var sketch = newSketch(context, id + "F25", { "sketchPlane" : qUnion([Q0])});
            skText(sketch, "E67", { "text": "OFF", "fontName": "AllertaStencil-Regular.ttf"});
            skText(sketch, "E68", { "text": "ON", "fontName": "AllertaStencil-Regular.ttf"});
            skLineSegment(sketch, "E69", {"start": v(-38, 38) * mm, "end": v(-38, 17.5) * mm});
            skLineSegment(sketch, "E70", {"start": v(-38, 38) * mm, "end": v(-38, 58.5) * mm});
            skPoint(sketch, "E71", {"position": v(-38, 17.5) * mm});
            skPoint(sketch, "E72", {"position": v(-38, 58.5) * mm});
            skPoint(sketch, "E73", {"position": v(-38, 38) * mm});
            skText(sketch, "E74", { "text": "12V", "fontName": "AllertaStencil-Regular.ttf"});
            skPoint(sketch, "E75", {"position": v(-7.38, -38) * mm});
            const initialGuessF25  = {"E67": [-0.034, 0.00674, 0, 1, 0.008], "E68": [-0.034, 0.05057, 0, 1, 0.008], "E74": [-0.00388, -0.0477, 0, 1, 0.008]};
            skSetInitialGuess(sketch, initialGuessF25);
            skSolve(sketch);
        }
        {
            var Q0;
            Q0 = qSketchRegion(id + "F25", true);
            extrude(context, id + "F26", {"entities" : qUnion([Q0]), "operationType" : NewBodyOperationType.REMOVE, "oppositeDirection" : true, "depth" : 1 * mm});
        }
        {
            var Q0;
            Q0=makeQuery(id+"F26.boolean.opBoolean","COPY",FACE,{"derivedFrom":makeQuery(id+"F26.opExtrude","CAP_FACE",FACE,{"disambiguationData":[OSD([sQuery(id+"F25.wireOp",EDGE,"E67.sketch_text.stroke-18"),sQuery(id+"F25.wireOp",EDGE,"E67.sketch_text.stroke-19"),sQuery(id+"F25.wireOp",EDGE,"E67.sketch_text.stroke-20"),sQuery(id+"F25.wireOp",EDGE,"E67.sketch_text.stroke-21"),sQuery(id+"F25.wireOp",EDGE,"E67.sketch_text.stroke-22"),sQuery(id+"F25.wireOp",EDGE,"E67.sketch_text.stroke-23"),sQuery(id+"F25.wireOp",EDGE,"E67.sketch_text.stroke-24"),sQuery(id+"F25.wireOp",EDGE,"E67.sketch_text.stroke-25"),sQuery(id+"F25.wireOp",EDGE,"E67.sketch_text.stroke-26"),sQuery(id+"F25.wireOp",EDGE,"E67.sketch_text.stroke-27"),sQuery(id+"F25.wireOp",EDGE,"E67.sketch_text.stroke-28"),sQuery(id+"F25.wireOp",EDGE,"E67.sketch_text.stroke-29"),sQuery(id+"F25.wireOp",EDGE,"E67.sketch_text.stroke-30"),sQuery(id+"F25.wireOp",EDGE,"E67.sketch_text.stroke-31"),sQuery(id+"F25.wireOp",EDGE,"E67.sketch_text.stroke-32"),sQuery(id+"F25.wireOp",EDGE,"E67.sketch_text.stroke-33"),sQuery(id+"F25.wireOp",EDGE,"E67.sketch_text.stroke-34"),sQuery(id+"F25.wireOp",EDGE,"E67.sketch_text.stroke-35")])],"isStart":false})});
            var Q1;
            Q1=makeQuery(id+"F26.boolean.opBoolean","COPY",FACE,{"derivedFrom":makeQuery(id+"F26.opExtrude","CAP_FACE",FACE,{"disambiguationData":[OSD([sQuery(id+"F25.wireOp",EDGE,"E67.sketch_text.stroke-0"),sQuery(id+"F25.wireOp",EDGE,"E67.sketch_text.stroke-1"),sQuery(id+"F25.wireOp",EDGE,"E67.sketch_text.stroke-2"),sQuery(id+"F25.wireOp",EDGE,"E67.sketch_text.stroke-3"),sQuery(id+"F25.wireOp",EDGE,"E67.sketch_text.stroke-4"),sQuery(id+"F25.wireOp",EDGE,"E67.sketch_text.stroke-5"),sQuery(id+"F25.wireOp",EDGE,"E67.sketch_text.stroke-6"),sQuery(id+"F25.wireOp",EDGE,"E67.sketch_text.stroke-7"),sQuery(id+"F25.wireOp",EDGE,"E67.sketch_text.stroke-8"),sQuery(id+"F25.wireOp",EDGE,"E67.sketch_text.stroke-9"),sQuery(id+"F25.wireOp",EDGE,"E67.sketch_text.stroke-10"),sQuery(id+"F25.wireOp",EDGE,"E67.sketch_text.stroke-11"),sQuery(id+"F25.wireOp",EDGE,"E67.sketch_text.stroke-12"),sQuery(id+"F25.wireOp",EDGE,"E67.sketch_text.stroke-13"),sQuery(id+"F25.wireOp",EDGE,"E67.sketch_text.stroke-14"),sQuery(id+"F25.wireOp",EDGE,"E67.sketch_text.stroke-15"),sQuery(id+"F25.wireOp",EDGE,"E67.sketch_text.stroke-16"),sQuery(id+"F25.wireOp",EDGE,"E67.sketch_text.stroke-17")])],"isStart":false})});
            var Q2;
            Q2=makeQuery(id+"F26.boolean.opBoolean","COPY",FACE,{"derivedFrom":makeQuery(id+"F26.opExtrude","CAP_FACE",FACE,{"disambiguationData":[OSD([sQuery(id+"F25.wireOp",EDGE,"E67.sketch_text.stroke-36"),sQuery(id+"F25.wireOp",EDGE,"E67.sketch_text.stroke-37"),sQuery(id+"F25.wireOp",EDGE,"E67.sketch_text.stroke-38"),sQuery(id+"F25.wireOp",EDGE,"E67.sketch_text.stroke-39")])],"isStart":false})});
            var Q3;
            Q3=makeQuery(id+"F26.boolean.opBoolean","COPY",FACE,{"derivedFrom":makeQuery(id+"F26.opExtrude","CAP_FACE",FACE,{"disambiguationData":[OSD([sQuery(id+"F25.wireOp",EDGE,"E67.sketch_text.stroke-40"),sQuery(id+"F25.wireOp",EDGE,"E67.sketch_text.stroke-41"),sQuery(id+"F25.wireOp",EDGE,"E67.sketch_text.stroke-42"),sQuery(id+"F25.wireOp",EDGE,"E67.sketch_text.stroke-43")])],"isStart":false})});
            var Q4;
            Q4=makeQuery(id+"F26.boolean.opBoolean","COPY",FACE,{"derivedFrom":makeQuery(id+"F26.opExtrude","CAP_FACE",FACE,{"disambiguationData":[OSD([sQuery(id+"F25.wireOp",EDGE,"E67.sketch_text.stroke-44"),sQuery(id+"F25.wireOp",EDGE,"E67.sketch_text.stroke-45"),sQuery(id+"F25.wireOp",EDGE,"E67.sketch_text.stroke-46"),sQuery(id+"F25.wireOp",EDGE,"E67.sketch_text.stroke-47")])],"isStart":false})});
            var Q5;
            Q5=makeQuery(id+"F26.boolean.opBoolean","COPY",FACE,{"derivedFrom":makeQuery(id+"F26.opExtrude","CAP_FACE",FACE,{"disambiguationData":[OSD([sQuery(id+"F25.wireOp",EDGE,"E67.sketch_text.stroke-48"),sQuery(id+"F25.wireOp",EDGE,"E67.sketch_text.stroke-49"),sQuery(id+"F25.wireOp",EDGE,"E67.sketch_text.stroke-50"),sQuery(id+"F25.wireOp",EDGE,"E67.sketch_text.stroke-51")])],"isStart":false})});
            var Q6;
            Q6=makeQuery(id+"F26.boolean.opBoolean","COPY",FACE,{"derivedFrom":makeQuery(id+"F26.opExtrude","CAP_FACE",FACE,{"disambiguationData":[OSD([sQuery(id+"F25.wireOp",EDGE,"E67.sketch_text.stroke-56"),sQuery(id+"F25.wireOp",EDGE,"E67.sketch_text.stroke-57"),sQuery(id+"F25.wireOp",EDGE,"E67.sketch_text.stroke-58"),sQuery(id+"F25.wireOp",EDGE,"E67.sketch_text.stroke-59")])],"isStart":false})});
            var Q7;
            Q7=makeQuery(id+"F26.boolean.opBoolean","COPY",FACE,{"derivedFrom":makeQuery(id+"F26.opExtrude","CAP_FACE",FACE,{"disambiguationData":[OSD([sQuery(id+"F25.wireOp",EDGE,"E67.sketch_text.stroke-52"),sQuery(id+"F25.wireOp",EDGE,"E67.sketch_text.stroke-53"),sQuery(id+"F25.wireOp",EDGE,"E67.sketch_text.stroke-54"),sQuery(id+"F25.wireOp",EDGE,"E67.sketch_text.stroke-55")])],"isStart":false})});
            var Q8;
            Q8=makeQuery(id+"F26.boolean.opBoolean","COPY",FACE,{"derivedFrom":makeQuery(id+"F26.opExtrude","CAP_FACE",FACE,{"disambiguationData":[OSD([sQuery(id+"F25.wireOp",EDGE,"E68.sketch_text.stroke-0"),sQuery(id+"F25.wireOp",EDGE,"E68.sketch_text.stroke-1"),sQuery(id+"F25.wireOp",EDGE,"E68.sketch_text.stroke-2"),sQuery(id+"F25.wireOp",EDGE,"E68.sketch_text.stroke-3"),sQuery(id+"F25.wireOp",EDGE,"E68.sketch_text.stroke-4"),sQuery(id+"F25.wireOp",EDGE,"E68.sketch_text.stroke-5"),sQuery(id+"F25.wireOp",EDGE,"E68.sketch_text.stroke-6"),sQuery(id+"F25.wireOp",EDGE,"E68.sketch_text.stroke-7"),sQuery(id+"F25.wireOp",EDGE,"E68.sketch_text.stroke-8"),sQuery(id+"F25.wireOp",EDGE,"E68.sketch_text.stroke-9"),sQuery(id+"F25.wireOp",EDGE,"E68.sketch_text.stroke-10"),sQuery(id+"F25.wireOp",EDGE,"E68.sketch_text.stroke-11"),sQuery(id+"F25.wireOp",EDGE,"E68.sketch_text.stroke-12"),sQuery(id+"F25.wireOp",EDGE,"E68.sketch_text.stroke-13"),sQuery(id+"F25.wireOp",EDGE,"E68.sketch_text.stroke-14"),sQuery(id+"F25.wireOp",EDGE,"E68.sketch_text.stroke-15"),sQuery(id+"F25.wireOp",EDGE,"E68.sketch_text.stroke-16"),sQuery(id+"F25.wireOp",EDGE,"E68.sketch_text.stroke-17")])],"isStart":false})});
            var Q9;
            Q9=makeQuery(id+"F26.boolean.opBoolean","COPY",FACE,{"derivedFrom":makeQuery(id+"F26.opExtrude","CAP_FACE",FACE,{"disambiguationData":[OSD([sQuery(id+"F25.wireOp",EDGE,"E68.sketch_text.stroke-18"),sQuery(id+"F25.wireOp",EDGE,"E68.sketch_text.stroke-19"),sQuery(id+"F25.wireOp",EDGE,"E68.sketch_text.stroke-20"),sQuery(id+"F25.wireOp",EDGE,"E68.sketch_text.stroke-21"),sQuery(id+"F25.wireOp",EDGE,"E68.sketch_text.stroke-22"),sQuery(id+"F25.wireOp",EDGE,"E68.sketch_text.stroke-23"),sQuery(id+"F25.wireOp",EDGE,"E68.sketch_text.stroke-24"),sQuery(id+"F25.wireOp",EDGE,"E68.sketch_text.stroke-25"),sQuery(id+"F25.wireOp",EDGE,"E68.sketch_text.stroke-26"),sQuery(id+"F25.wireOp",EDGE,"E68.sketch_text.stroke-27"),sQuery(id+"F25.wireOp",EDGE,"E68.sketch_text.stroke-28"),sQuery(id+"F25.wireOp",EDGE,"E68.sketch_text.stroke-29"),sQuery(id+"F25.wireOp",EDGE,"E68.sketch_text.stroke-30"),sQuery(id+"F25.wireOp",EDGE,"E68.sketch_text.stroke-31"),sQuery(id+"F25.wireOp",EDGE,"E68.sketch_text.stroke-32"),sQuery(id+"F25.wireOp",EDGE,"E68.sketch_text.stroke-33"),sQuery(id+"F25.wireOp",EDGE,"E68.sketch_text.stroke-34"),sQuery(id+"F25.wireOp",EDGE,"E68.sketch_text.stroke-35")])],"isStart":false})});
            var Q10;
            Q10=makeQuery(id+"F26.boolean.opBoolean","COPY",FACE,{"derivedFrom":makeQuery(id+"F26.opExtrude","CAP_FACE",FACE,{"disambiguationData":[OSD([sQuery(id+"F25.wireOp",EDGE,"E68.sketch_text.stroke-43"),sQuery(id+"F25.wireOp",EDGE,"E68.sketch_text.stroke-44"),sQuery(id+"F25.wireOp",EDGE,"E68.sketch_text.stroke-45"),sQuery(id+"F25.wireOp",EDGE,"E68.sketch_text.stroke-46")])],"isStart":false})});
            var Q11;
            Q11=makeQuery(id+"F26.boolean.opBoolean","COPY",FACE,{"derivedFrom":makeQuery(id+"F26.opExtrude","CAP_FACE",FACE,{"disambiguationData":[OSD([sQuery(id+"F25.wireOp",EDGE,"E68.sketch_text.stroke-36"),sQuery(id+"F25.wireOp",EDGE,"E68.sketch_text.stroke-37"),sQuery(id+"F25.wireOp",EDGE,"E68.sketch_text.stroke-38"),sQuery(id+"F25.wireOp",EDGE,"E68.sketch_text.stroke-39"),sQuery(id+"F25.wireOp",EDGE,"E68.sketch_text.stroke-40"),sQuery(id+"F25.wireOp",EDGE,"E68.sketch_text.stroke-41"),sQuery(id+"F25.wireOp",EDGE,"E68.sketch_text.stroke-42")])],"isStart":false})});
            var Q12;
            Q12=makeQuery(id+"F26.boolean.opBoolean","COPY",FACE,{"derivedFrom":makeQuery(id+"F26.opExtrude","CAP_FACE",FACE,{"disambiguationData":[OSD([sQuery(id+"F25.wireOp",EDGE,"E74.sketch_text.stroke-0"),sQuery(id+"F25.wireOp",EDGE,"E74.sketch_text.stroke-1"),sQuery(id+"F25.wireOp",EDGE,"E74.sketch_text.stroke-2"),sQuery(id+"F25.wireOp",EDGE,"E74.sketch_text.stroke-3"),sQuery(id+"F25.wireOp",EDGE,"E74.sketch_text.stroke-4"),sQuery(id+"F25.wireOp",EDGE,"E74.sketch_text.stroke-5"),sQuery(id+"F25.wireOp",EDGE,"E74.sketch_text.stroke-6")])],"isStart":false})});
            var Q13;
            Q13=makeQuery(id+"F26.boolean.opBoolean","COPY",FACE,{"derivedFrom":makeQuery(id+"F26.opExtrude","CAP_FACE",FACE,{"disambiguationData":[OSD([sQuery(id+"F25.wireOp",EDGE,"E74.sketch_text.stroke-7"),sQuery(id+"F25.wireOp",EDGE,"E74.sketch_text.stroke-8"),sQuery(id+"F25.wireOp",EDGE,"E74.sketch_text.stroke-9"),sQuery(id+"F25.wireOp",EDGE,"E74.sketch_text.stroke-10"),sQuery(id+"F25.wireOp",EDGE,"E74.sketch_text.stroke-11"),sQuery(id+"F25.wireOp",EDGE,"E74.sketch_text.stroke-12"),sQuery(id+"F25.wireOp",EDGE,"E74.sketch_text.stroke-13"),sQuery(id+"F25.wireOp",EDGE,"E74.sketch_text.stroke-14"),sQuery(id+"F25.wireOp",EDGE,"E74.sketch_text.stroke-15"),sQuery(id+"F25.wireOp",EDGE,"E74.sketch_text.stroke-16"),sQuery(id+"F25.wireOp",EDGE,"E74.sketch_text.stroke-17"),sQuery(id+"F25.wireOp",EDGE,"E74.sketch_text.stroke-18"),sQuery(id+"F25.wireOp",EDGE,"E74.sketch_text.stroke-19"),sQuery(id+"F25.wireOp",EDGE,"E74.sketch_text.stroke-20"),sQuery(id+"F25.wireOp",EDGE,"E74.sketch_text.stroke-21"),sQuery(id+"F25.wireOp",EDGE,"E74.sketch_text.stroke-22"),sQuery(id+"F25.wireOp",EDGE,"E74.sketch_text.stroke-23"),sQuery(id+"F25.wireOp",EDGE,"E74.sketch_text.stroke-24"),sQuery(id+"F25.wireOp",EDGE,"E74.sketch_text.stroke-25"),sQuery(id+"F25.wireOp",EDGE,"E74.sketch_text.stroke-26"),sQuery(id+"F25.wireOp",EDGE,"E74.sketch_text.stroke-27"),sQuery(id+"F25.wireOp",EDGE,"E74.sketch_text.stroke-28"),sQuery(id+"F25.wireOp",EDGE,"E74.sketch_text.stroke-29"),sQuery(id+"F25.wireOp",EDGE,"E74.sketch_text.stroke-30"),sQuery(id+"F25.wireOp",EDGE,"E74.sketch_text.stroke-31"),sQuery(id+"F25.wireOp",EDGE,"E74.sketch_text.stroke-32"),sQuery(id+"F25.wireOp",EDGE,"E74.sketch_text.stroke-33"),sQuery(id+"F25.wireOp",EDGE,"E74.sketch_text.stroke-34"),sQuery(id+"F25.wireOp",EDGE,"E74.sketch_text.stroke-35"),sQuery(id+"F25.wireOp",EDGE,"E74.sketch_text.stroke-36"),sQuery(id+"F25.wireOp",EDGE,"E74.sketch_text.stroke-37"),sQuery(id+"F25.wireOp",EDGE,"E74.sketch_text.stroke-38"),sQuery(id+"F25.wireOp",EDGE,"E74.sketch_text.stroke-39")])],"isStart":false})});
            var Q14;
            Q14=makeQuery(id+"F26.boolean.opBoolean","COPY",FACE,{"derivedFrom":makeQuery(id+"F26.opExtrude","CAP_FACE",FACE,{"disambiguationData":[OSD([sQuery(id+"F25.wireOp",EDGE,"E74.sketch_text.stroke-40"),sQuery(id+"F25.wireOp",EDGE,"E74.sketch_text.stroke-41"),sQuery(id+"F25.wireOp",EDGE,"E74.sketch_text.stroke-42"),sQuery(id+"F25.wireOp",EDGE,"E74.sketch_text.stroke-43"),sQuery(id+"F25.wireOp",EDGE,"E74.sketch_text.stroke-44")])],"isStart":false})});
            var Q15;
            Q15=makeQuery(id+"F26.boolean.opBoolean","COPY",FACE,{"derivedFrom":makeQuery(id+"F26.opExtrude","CAP_FACE",FACE,{"disambiguationData":[OSD([sQuery(id+"F25.wireOp",EDGE,"E74.sketch_text.stroke-45"),sQuery(id+"F25.wireOp",EDGE,"E74.sketch_text.stroke-46"),sQuery(id+"F25.wireOp",EDGE,"E74.sketch_text.stroke-47"),sQuery(id+"F25.wireOp",EDGE,"E74.sketch_text.stroke-48"),sQuery(id+"F25.wireOp",EDGE,"E74.sketch_text.stroke-49")])],"isStart":false})});
            fillet(context, id + "F27", {"entities" : qUnion([Q0, Q1, Q2, Q3, Q4, Q5, Q6, Q7, Q8, Q9, Q10, Q11, Q12, Q13, Q14, Q15]), "radius" : .4 * mm, "tangentPropagation" : true, "allowEdgeOverflow" : false});
        }
    });
